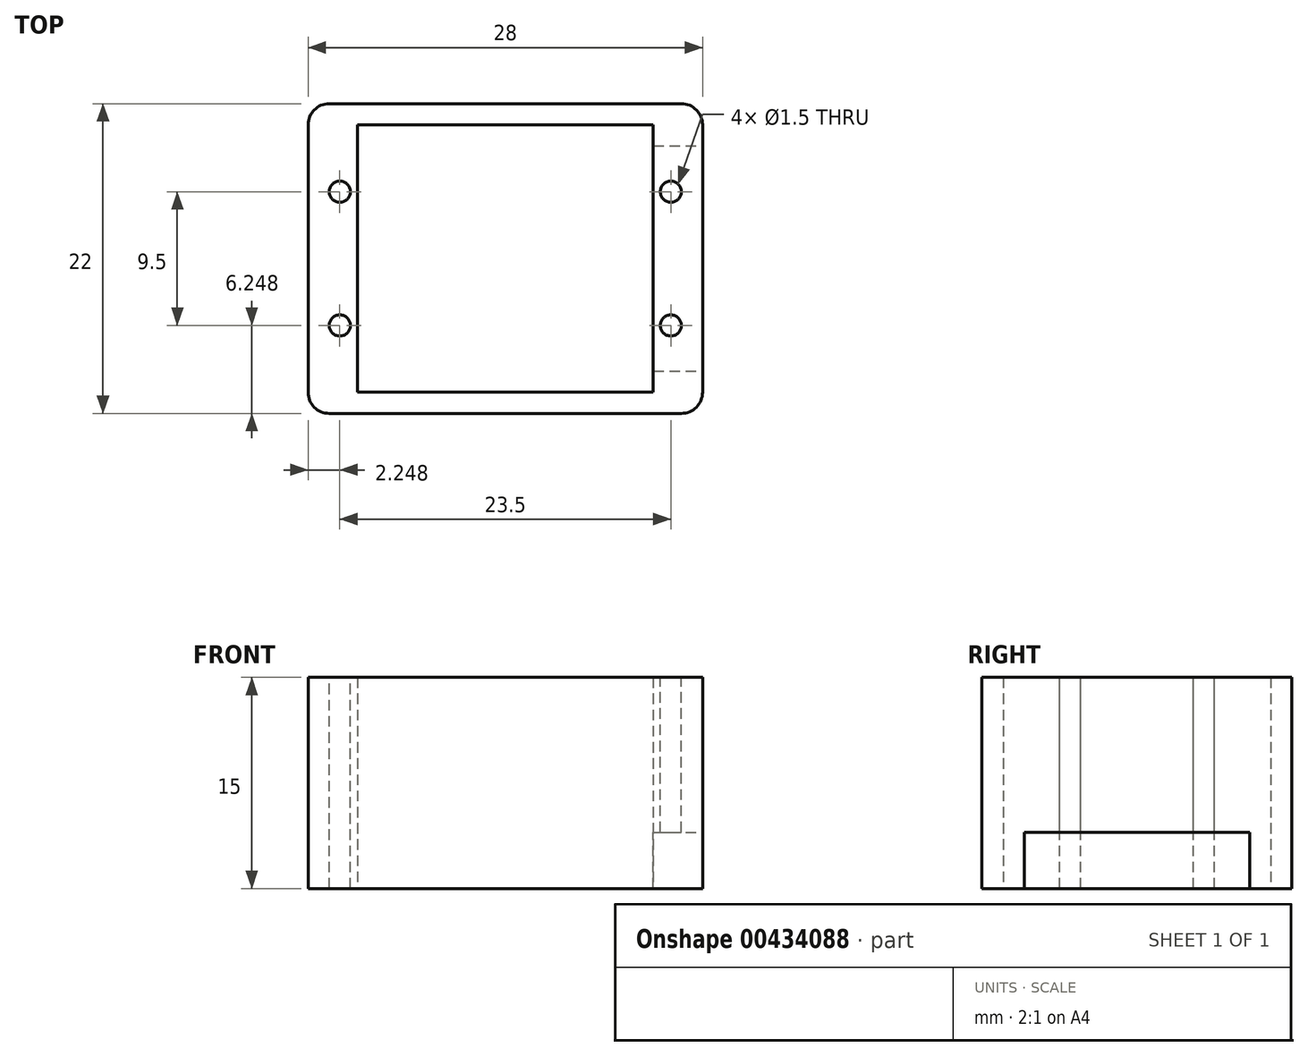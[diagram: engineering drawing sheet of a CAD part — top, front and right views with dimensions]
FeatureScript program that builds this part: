
annotation { "Feature Type Name" : "Feature", "Feature Type Description" : "" }
export const myFeature = defineFeature(function(context is Context, id is Id, definition is map)
    precondition{}
    {
        {
            var Q0;
            Q0=qCreatedBy(makeId("Top.planeOp"),FACE);
            var sketch = newSketch(context, id + "F0", { "sketchPlane" : qUnion([Q0])});
            skLineSegment(sketch, "E0.bottom", {"start": v(-15.26, 10.35) * mm, "end": v(12.74, 10.35) * mm});
            skLineSegment(sketch, "E0.top", {"start": v(-15.26, -11.65) * mm, "end": v(12.74, -11.65) * mm});
            skLineSegment(sketch, "E0.left", {"start": v(-15.26, 10.35) * mm, "end": v(-15.26, -11.65) * mm});
            skLineSegment(sketch, "E0.right", {"start": v(12.74, 10.35) * mm, "end": v(12.74, -11.65) * mm});
            skLineSegment(sketch, "E1.0", {"start": v(-11.76, 8.85) * mm, "end": v(5.74, 8.85) * mm});
            skLineSegment(sketch, "E2.0", {"start": v(-11.76, -10.15) * mm, "end": v(5.74, -10.15) * mm});
            skLineSegment(sketch, "E3.0", {"start": v(-11.76, 8.85) * mm, "end": v(-11.76, -10.15) * mm});
            skLineSegment(sketch, "E4.0", {"start": v(9.24, 8.85) * mm, "end": v(9.24, -10.15) * mm});
            skLineSegment(sketch, "E5.bottom", {"start": v(-11.76, 8.85) * mm, "end": v(9.24, 8.85) * mm});
            skLineSegment(sketch, "E5.top", {"start": v(-11.76, -10.15) * mm, "end": v(9.24, -10.15) * mm});
            skSolve(sketch);
        }
        {
            var Q0;
            Q0=qSketchRegion(id+"F0",true);
            extrude(context, id + "F1", {"entities" : qUnion([Q0]), "depth" : 15 * mm, "offsetDistance" : 25 * mm});
        }
        {
            var Q0;
            Q0=makeQuery(id+"F1.opExtrude","SWEPT_FACE",FACE,{"disambiguationData":[OSD([sQuery(id+"F0.wireOp",EDGE,"E0.right")])]});
            var sketch = newSketch(context, id + "F2", { "sketchPlane" : qUnion([Q0])});
            skLineSegment(sketch, "E6", {"start": v(-0.65, 15) * mm, "end": v(-0.65, -4.28) * mm, "construction": true});
            skPoint(sketch, "E7.right.end.orphan", {"position": v(1.87, 4) * mm});
            skLineSegment(sketch, "E8.0", {"start": v(-8.65, 4) * mm, "end": v(-8.65, 0) * mm, "construction": true});
            skLineSegment(sketch, "E9.0", {"start": v(7.35, 4) * mm, "end": v(7.35, 0) * mm, "construction": true});
            skLineSegment(sketch, "E10.bottom", {"start": v(-8.65, 0) * mm, "end": v(7.35, 0) * mm});
            skLineSegment(sketch, "E10.top", {"start": v(-8.65, 4) * mm, "end": v(7.35, 4) * mm});
            skLineSegment(sketch, "E10.left", {"start": v(-8.65, 0) * mm, "end": v(-8.65, 4) * mm});
            skLineSegment(sketch, "E10.right", {"start": v(7.35, 0) * mm, "end": v(7.35, 4) * mm});
            skSolve(sketch);
        }
        {
            var Q0;
            Q0=makeQuery(id+"F1.opExtrude","SWEPT_EDGE",EDGE,{"disambiguationData":[OSD([sQuery(id+"F0.wireOp",EDGE,"E0.bottom"),sQuery(id+"F0.wireOp",EDGE,"E0.right")])]});
            var Q1;
            Q1=makeQuery(id+"F1.opExtrude","SWEPT_EDGE",EDGE,{"disambiguationData":[OSD([sQuery(id+"F0.wireOp",EDGE,"E0.top"),sQuery(id+"F0.wireOp",EDGE,"E0.right")])]});
            var Q2;
            Q2=makeQuery(id+"F1.opExtrude","SWEPT_EDGE",EDGE,{"disambiguationData":[OSD([sQuery(id+"F0.wireOp",EDGE,"E0.top"),sQuery(id+"F0.wireOp",EDGE,"E0.left")])]});
            var Q3;
            Q3=makeQuery(id+"F1.opExtrude","SWEPT_EDGE",EDGE,{"disambiguationData":[OSD([sQuery(id+"F0.wireOp",EDGE,"E0.bottom"),sQuery(id+"F0.wireOp",EDGE,"E0.left")])]});
            fillet(context, id + "F3", {"entities" : qUnion([Q0, Q1, Q2, Q3]), "radius" : 1.5 * mm, "tangentPropagation" : true, "allowEdgeOverflow" : false});
        }
        {
            var Q0;
            Q0=makeQuery(id+"F1.opExtrude","CAP_FACE",FACE,{"disambiguationData":[OSD([sQuery(id+"F0.wireOp",EDGE,"E0.bottom"),sQuery(id+"F0.wireOp",EDGE,"E0.top"),sQuery(id+"F0.wireOp",EDGE,"E0.left"),sQuery(id+"F0.wireOp",EDGE,"E0.right"),sQuery(id+"F0.wireOp",EDGE,"E5.bottom"),sQuery(id+"F0.wireOp",EDGE,"E5.top"),sQuery(id+"F0.wireOp",EDGE,"E3.0"),sQuery(id+"F0.wireOp",EDGE,"E4.0")])],"isStart":false});
            var sketch = newSketch(context, id + "F4", { "sketchPlane" : qUnion([Q0])});
            skLineSegment(sketch, "E11", {"start": v(-1.26, 8.85) * mm, "end": v(-1.26, -10.15) * mm, "construction": true});
            skLineSegment(sketch, "E12", {"start": v(-15.26, -0.65) * mm, "end": v(12.74, -0.65) * mm, "construction": true});
            skLineSegment(sketch, "E13.0", {"start": v(-15.26, -5.4) * mm, "end": v(10.74, -5.4) * mm, "construction": true});
            skLineSegment(sketch, "E14.0", {"start": v(-15.26, 4.1) * mm, "end": v(10.74, 4.1) * mm, "construction": true});
            skLineSegment(sketch, "E15.0", {"start": v(-13.01, 6.85) * mm, "end": v(-13.01, -8.15) * mm, "construction": true});
            skLineSegment(sketch, "E16.0", {"start": v(10.49, 6.85) * mm, "end": v(10.49, -8.15) * mm, "construction": true});
            skCircle(sketch, "E17", {"center": v(-13.01, 4.1) * mm, "radius": 0.75 * mm});
            skCircle(sketch, "E18", {"center": v(-13.01, -5.4) * mm, "radius": 0.75 * mm});
            skCircle(sketch, "E19", {"center": v(10.49, 4.1) * mm, "radius": 0.75 * mm});
            skCircle(sketch, "E20", {"center": v(10.49, -5.4) * mm, "radius": 0.75 * mm});
            skSolve(sketch);
        }
        {
            var Q0;
            Q0=sQuery(id+"F4.wireOp",VERTEX,"E17.center");
            var Q1;
            Q1=makeQuery(id+"F1.opExtrude","SWEPT_BODY",BODY,{"disambiguationData":[OSD([sQuery(id+"F0.wireOp",EDGE,"E0.bottom"),sQuery(id+"F0.wireOp",EDGE,"E0.top"),sQuery(id+"F0.wireOp",EDGE,"E0.left"),sQuery(id+"F0.wireOp",EDGE,"E0.right"),sQuery(id+"F0.wireOp",EDGE,"E5.bottom"),sQuery(id+"F0.wireOp",EDGE,"E5.top"),sQuery(id+"F0.wireOp",EDGE,"E3.0"),sQuery(id+"F0.wireOp",EDGE,"E4.0")])]});
            hole(context, id + "F5", {"style" : HoleStyle.SIMPLE, "endStyle" : HoleEndStyle.THROUGH, "holeDiameter" : 1.5 * mm, "isTappedThrough" : true, "tappedDepth" : 12 * mm, "tapClearance" : 3, "locations" : qUnion([Q0]), "scope" : qUnion([Q1])});
        }
        {
            var Q0;
            Q0=sQuery(id+"F4.wireOp",VERTEX,"E18.center");
            var Q1;
            Q1=makeQuery(id+"F1.opExtrude","SWEPT_BODY",BODY,{"disambiguationData":[OSD([sQuery(id+"F0.wireOp",EDGE,"E0.bottom"),sQuery(id+"F0.wireOp",EDGE,"E0.top"),sQuery(id+"F0.wireOp",EDGE,"E0.left"),sQuery(id+"F0.wireOp",EDGE,"E0.right"),sQuery(id+"F0.wireOp",EDGE,"E5.bottom"),sQuery(id+"F0.wireOp",EDGE,"E5.top"),sQuery(id+"F0.wireOp",EDGE,"E3.0"),sQuery(id+"F0.wireOp",EDGE,"E4.0")])]});
            hole(context, id + "F6", {"style" : HoleStyle.SIMPLE, "endStyle" : HoleEndStyle.THROUGH, "holeDiameter" : 1.5 * mm, "isTappedThrough" : true, "tappedDepth" : 12 * mm, "tapClearance" : 3, "locations" : qUnion([Q0]), "scope" : qUnion([Q1])});
        }
        {
            var Q0;
            Q0=sQuery(id+"F4.wireOp",VERTEX,"E20.center");
            var Q1;
            Q1=makeQuery(id+"F1.opExtrude","SWEPT_BODY",BODY,{"disambiguationData":[OSD([sQuery(id+"F0.wireOp",EDGE,"E0.bottom"),sQuery(id+"F0.wireOp",EDGE,"E0.top"),sQuery(id+"F0.wireOp",EDGE,"E0.left"),sQuery(id+"F0.wireOp",EDGE,"E0.right"),sQuery(id+"F0.wireOp",EDGE,"E5.bottom"),sQuery(id+"F0.wireOp",EDGE,"E5.top"),sQuery(id+"F0.wireOp",EDGE,"E3.0"),sQuery(id+"F0.wireOp",EDGE,"E4.0")])]});
            hole(context, id + "F7", {"style" : HoleStyle.SIMPLE, "endStyle" : HoleEndStyle.THROUGH, "holeDiameter" : 1.5 * mm, "isTappedThrough" : true, "tappedDepth" : 12 * mm, "tapClearance" : 3, "locations" : qUnion([Q0]), "scope" : qUnion([Q1])});
        }
        {
            var Q0;
            Q0=sQuery(id+"F4.wireOp",VERTEX,"E19.center");
            var Q1;
            Q1=makeQuery(id+"F1.opExtrude","SWEPT_BODY",BODY,{"disambiguationData":[OSD([sQuery(id+"F0.wireOp",EDGE,"E0.bottom"),sQuery(id+"F0.wireOp",EDGE,"E0.top"),sQuery(id+"F0.wireOp",EDGE,"E0.left"),sQuery(id+"F0.wireOp",EDGE,"E0.right"),sQuery(id+"F0.wireOp",EDGE,"E5.bottom"),sQuery(id+"F0.wireOp",EDGE,"E5.top"),sQuery(id+"F0.wireOp",EDGE,"E3.0"),sQuery(id+"F0.wireOp",EDGE,"E4.0")])]});
            hole(context, id + "F8", {"style" : HoleStyle.SIMPLE, "endStyle" : HoleEndStyle.THROUGH, "holeDiameter" : 1.5 * mm, "isTappedThrough" : true, "tappedDepth" : 12 * mm, "tapClearance" : 3, "locations" : qUnion([Q0]), "scope" : qUnion([Q1])});
        }
        {
            var Q0;
            Q0=makeQuery(id+"F2.imprint","IMPRINT",FACE,{"disambiguationData":[TD([[makeQuery(id+"F2.imprint","IMPRINT",EDGE,{"derivedFrom":sQuery(id+"F2.wireOp",EDGE,"E10.bottom")}),-1.0]])]});
            extrude(context, id + "F9", {"entities" : qUnion([Q0]), "operationType" : NewBodyOperationType.REMOVE, "oppositeDirection" : true, "depth" : 10 * mm, "offsetDistance" : 25 * mm});
        }
    });
